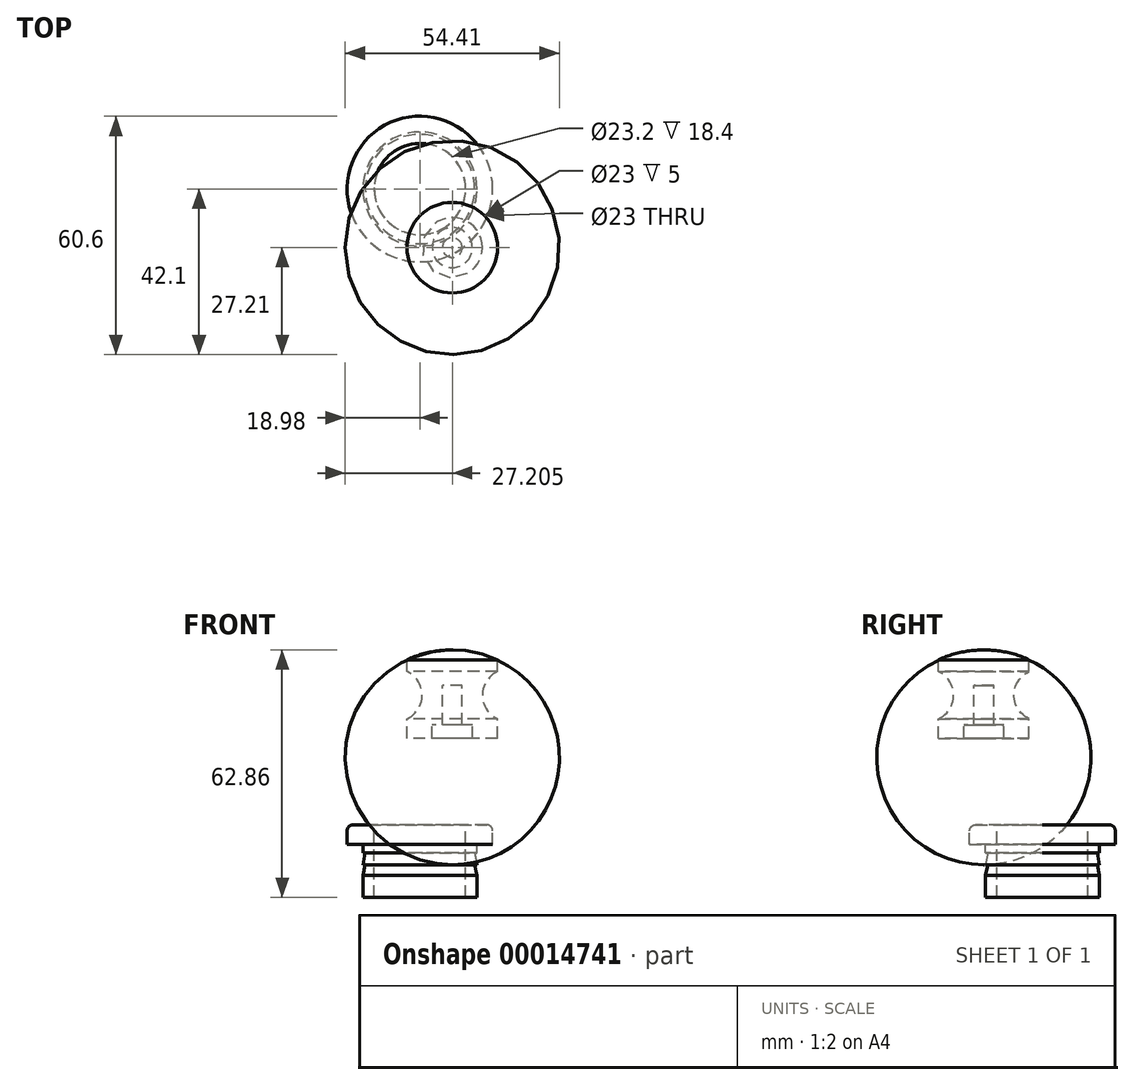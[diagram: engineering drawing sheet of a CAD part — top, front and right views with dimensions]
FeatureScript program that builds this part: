
annotation { "Feature Type Name" : "Feature", "Feature Type Description" : "" }
export const myFeature = defineFeature(function(context is Context, id is Id, definition is map)
    precondition{}
    {
        {
            var Q0;
            Q0=qCreatedBy(makeId("Front.planeOp"),FACE);
            var sketch = newSketch(context, id + "F0", { "sketchPlane" : qUnion([Q0])});
            skLineSegment(sketch, "E0", {"start": v(19.72, -14.8) * mm, "end": v(13.32, -14.8) * mm});
            skLineSegment(sketch, "E1", {"start": v(19.72, 5.2) * mm, "end": v(19.72, 2.2) * mm});
            skLineSegment(sketch, "E2", {"start": v(19.72, -14.8) * mm, "end": v(19.72, -9.8) * mm});
            skArc(sketch, "E3", {"start": v(19.72, 2.2) * mm, "mid": v(15.89, -3.8) * mm, "end": v(19.72, -9.8) * mm});
            skLineSegment(sketch, "E4", {"start": v(8.22, -1.3) * mm, "end": v(10.72, -1.3) * mm});
            skLineSegment(sketch, "E5", {"start": v(10.72, -1.3) * mm, "end": v(10.72, -11.3) * mm});
            skLineSegment(sketch, "E6", {"start": v(13.32, -14.8) * mm, "end": v(13.32, -11.3) * mm});
            skLineSegment(sketch, "E7", {"start": v(13.32, -11.3) * mm, "end": v(10.72, -11.3) * mm});
            skArc(sketch, "E8", {"start": v(19.72, 5.2) * mm, "mid": v(14.11, 7.07) * mm, "end": v(8.22, 7.7) * mm});
            skPoint(sketch, "E9.start.orphan", {"position": v(8.22, 5.2) * mm});
            skLineSegment(sketch, "E10", {"start": v(8.22, 7.7) * mm, "end": v(8.22, -1.3) * mm});
            skSolve(sketch);
        }
        {
            var Q0;
            Q0=makeQuery(id+"F0.imprint","IMPRINT",FACE,{"disambiguationData":[TD([[makeQuery(id+"F0.imprint","IMPRINT",EDGE,{"derivedFrom":sQuery(id+"F0.wireOp",EDGE,"E0")}),-1.0]])]});
            var Q1;
            Q1=sQuery(id+"F0.wireOp",EDGE,"E10");
            revolve(context, id + "F1", {"entities" : qUnion([Q0]), "axis" : qUnion([Q1]), "revolveType" : RevolveType.FULL});
        }
        {
            var Q0;
            Q0=qCreatedBy(makeId("Right.planeOp"),FACE);
            var sketch = newSketch(context, id + "F2", { "sketchPlane" : qUnion([Q0])});
            skLineSegment(sketch, "E11", {"start": v(14.89, 11.76) * mm, "end": v(14.89, 5.98) * mm, "construction": true});
            skLineSegment(sketch, "E12", {"start": v(26.49, 5.98) * mm, "end": v(26.49, -7.42) * mm});
            skLineSegment(sketch, "E13", {"start": v(29.39, 5.98) * mm, "end": v(29.39, 3.87) * mm});
            skLineSegment(sketch, "E14", {"start": v(29.39, -7.42) * mm, "end": v(26.49, -7.42) * mm});
            skLineSegment(sketch, "E15", {"start": v(26.49, 5.98) * mm, "end": v(26.49, 10.98) * mm});
            skLineSegment(sketch, "E16", {"start": v(29.39, 5.98) * mm, "end": v(33.39, 5.98) * mm});
            skLineSegment(sketch, "E17", {"start": v(29.39, 3.87) * mm, "end": v(28.8, 3.87) * mm});
            skLineSegment(sketch, "E18", {"start": v(28.8, 3.87) * mm, "end": v(29.39, 0.83) * mm});
            skLineSegment(sketch, "E19", {"start": v(28.8, 0.83) * mm, "end": v(29.39, 0.83) * mm});
            skLineSegment(sketch, "E20", {"start": v(28.8, 0.83) * mm, "end": v(29.39, -1.84) * mm});
            skLineSegment(sketch, "E21.trimOffspring", {"start": v(29.39, -1.84) * mm, "end": v(29.39, -7.42) * mm});
            skPoint(sketch, "E22.end.orphan", {"position": v(14.89, -7.42) * mm});
            skLineSegment(sketch, "E23.trimOffspring", {"start": v(14.89, -7.42) * mm, "end": v(14.89, -15.04) * mm, "construction": true});
            skLineSegment(sketch, "E24", {"start": v(14.89, 5.98) * mm, "end": v(14.89, -7.42) * mm, "construction": true});
            skLineSegment(sketch, "E25", {"start": v(26.49, 10.98) * mm, "end": v(31.89, 10.98) * mm});
            skLineSegment(sketch, "E26", {"start": v(33.39, 5.98) * mm, "end": v(33.39, 9.48) * mm});
            skPoint(sketch, "E27.visualSharp", {"position": v(33.39, 10.98) * mm});
            skArc(sketch, "E27.filletArc", {"start": v(33.39, 9.48) * mm, "mid": v(32.95, 10.54) * mm, "end": v(31.89, 10.98) * mm});
            skSolve(sketch);
        }
        {
            var Q0;
            Q0=makeQuery(id+"F2.imprint","IMPRINT",FACE,{"disambiguationData":[TD([[makeQuery(id+"F2.imprint","IMPRINT",EDGE,{"derivedFrom":sQuery(id+"F2.wireOp",EDGE,"E12")}),1.0]])]});
            var Q1;
            Q1=sQuery(id+"F2.wireOp",EDGE,"E24");
            revolve(context, id + "F3", {"entities" : qUnion([Q0]), "axis" : qUnion([Q1]), "revolveType" : RevolveType.FULL});
        }
        {
            var Q0;
            Q0=makeQuery(id+"F1.opRevolve","SWEPT_BODY",BODY,{"disambiguationData":[OSD([sQuery(id+"F0.wireOp",EDGE,"E0"),sQuery(id+"F0.wireOp",EDGE,"E1"),sQuery(id+"F0.wireOp",EDGE,"E2"),sQuery(id+"F0.wireOp",EDGE,"E3"),sQuery(id+"F0.wireOp",EDGE,"E4"),sQuery(id+"F0.wireOp",EDGE,"E5"),sQuery(id+"F0.wireOp",EDGE,"E6"),sQuery(id+"F0.wireOp",EDGE,"E7"),sQuery(id+"F0.wireOp",EDGE,"E8"),sQuery(id+"F0.wireOp",EDGE,"E10")])]});
            transform(context, id + "F4", {"entities" : qUnion([Q0]), "transformType" : TransformType.TRANSLATION_3D, "dx" : 0 * mm, "dy" : 0 * mm, "dz" : 27.74 * mm, "makeCopy" : false});
        }
        {
            var Q0;
            Q0=makeQuery(id+"F1.opRevolve","SWEPT_BODY",BODY,{"disambiguationData":[OSD([sQuery(id+"F0.wireOp",EDGE,"E0"),sQuery(id+"F0.wireOp",EDGE,"E1"),sQuery(id+"F0.wireOp",EDGE,"E2"),sQuery(id+"F0.wireOp",EDGE,"E3"),sQuery(id+"F0.wireOp",EDGE,"E4"),sQuery(id+"F0.wireOp",EDGE,"E5"),sQuery(id+"F0.wireOp",EDGE,"E6"),sQuery(id+"F0.wireOp",EDGE,"E7"),sQuery(id+"F0.wireOp",EDGE,"E8"),sQuery(id+"F0.wireOp",EDGE,"E10")])]});
            transform(context, id + "F5", {"entities" : qUnion([Q0]), "transformType" : TransformType.TRANSLATION_3D, "dx" : 0 * mm, "dy" : 0 * mm, "dz" : 20 * mm, "makeCopy" : false});
        }
    });
